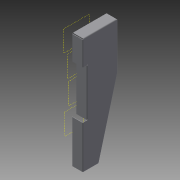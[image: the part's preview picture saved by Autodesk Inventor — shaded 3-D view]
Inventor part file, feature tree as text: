
AUTODESK INVENTOR PART (.ipt)
format: ipt  version: 2015 (Build 190159000, 159)  size: 190,464 bytes
history: native  units: mm
features: reference x8, sheet_metal_op x4, sketch x3, other x2, mirror x1
ambient origin geometry x8: Origin, YZ Plane, XZ Plane, XY Plane, X Axis, Y Axis, Z Axis, Center Point
bodies: Solid1 (feature_tree)
feature tree (18):
  sheet_metal_op  "Face1"
  sketch  "Sketch3"  dims[d16=445.0mm]
  sheet_metal_op  "Flange4"
  mirror  "Mirror1"
  sketch  "Sketch1"  dims[d1=1.6mm]
  reference  "Reference1"
  reference  "Reference2"
  other  "Plate1"
  reference  "Reference3"
  reference  "Reference4"
  reference  "Reference5"
  reference  "Reference6"
  reference  "Reference7"
  reference  "Reference8"
  sketch  "Sketch6"  dims[d17=35.0mm d18=50.0mm d19=3.922832mm d40=5.0mm d41=48.571429mm d42=5.0mm d43=5.0mm d44=1.6mm d45=0.8mm d46=3.2mm d47=1.6mm d48=40.0mm d49=90.0deg d50=1.6mm d51=6.4mm d52=1.6mm d53=1.6mm]
  other  "Plate5"
  sheet_metal_op  "Bend4"
  sheet_metal_op  "Corner4"
